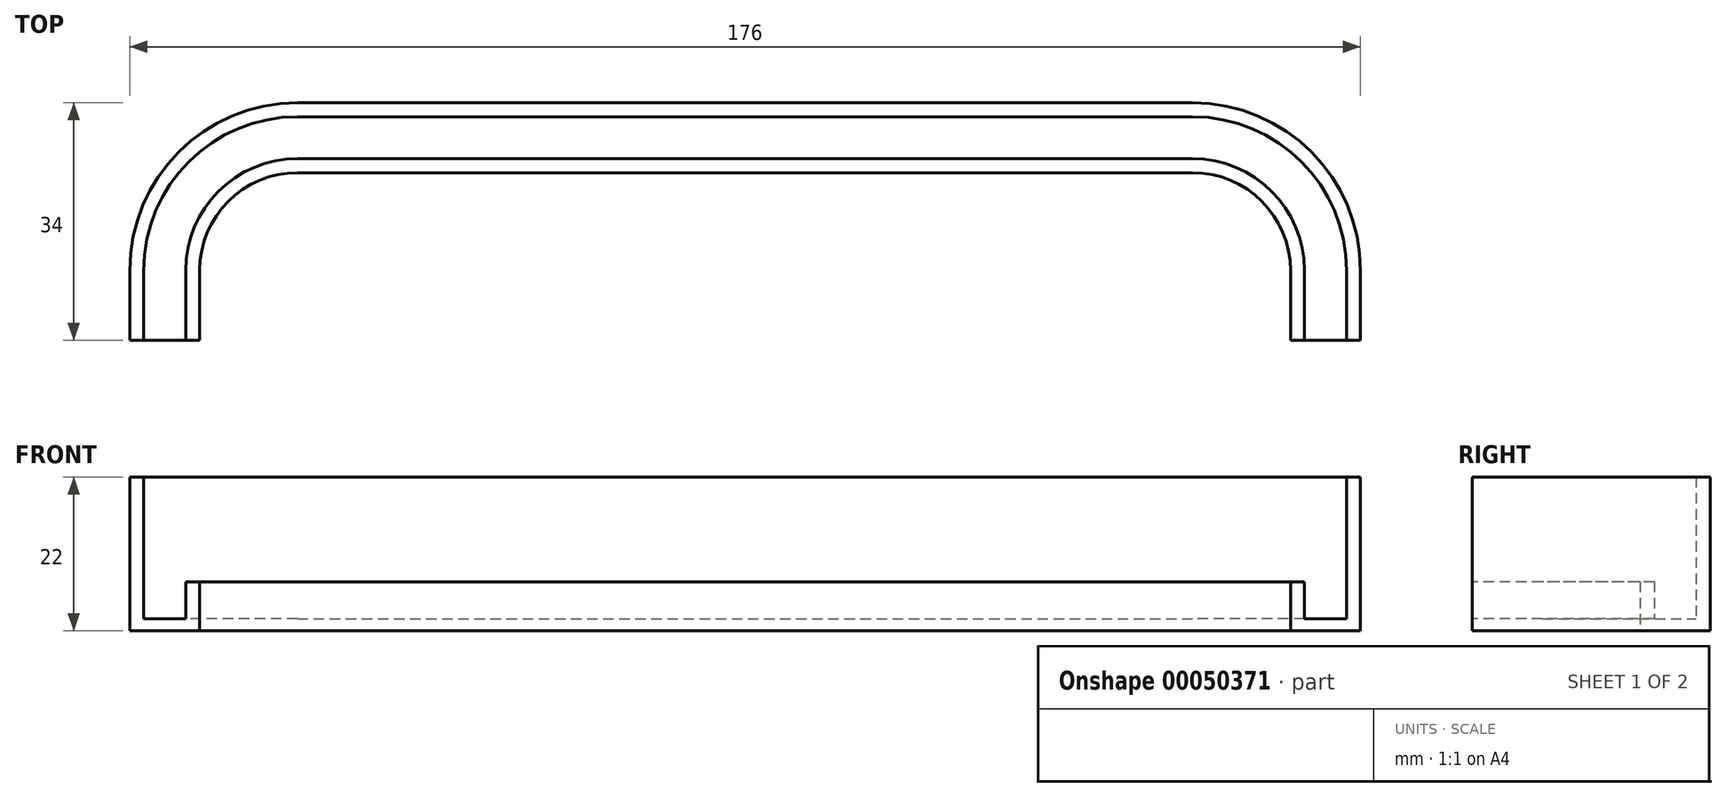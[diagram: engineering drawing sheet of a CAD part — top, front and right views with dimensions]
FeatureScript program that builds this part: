
annotation { "Feature Type Name" : "Feature", "Feature Type Description" : "" }
export const myFeature = defineFeature(function(context is Context, id is Id, definition is map)
    precondition{}
    {
        {
            var Q0;
            Q0=qCreatedBy(makeId("Top.planeOp"),FACE);
            var sketch = newSketch(context, id + "F0", { "sketchPlane" : qUnion([Q0])});
            skLineSegment(sketch, "E0", {"start": v(0, 0) * mm, "end": v(128, 0) * mm});
            skArc(sketch, "E1", {"start": v(0, 0) * mm, "mid": v(-9.9, -4.1) * mm, "end": v(-14, -14) * mm});
            skArc(sketch, "E2", {"start": v(128, 0) * mm, "mid": v(137.9, -4.1) * mm, "end": v(142, -14) * mm});
            skLineSegment(sketch, "E3", {"start": v(-14, -14) * mm, "end": v(-14, -24) * mm});
            skLineSegment(sketch, "E4", {"start": v(142, -14) * mm, "end": v(142, -24) * mm});
            skLineSegment(sketch, "E5.0", {"start": v(-16, -14) * mm, "end": v(-16, -24) * mm});
            skLineSegment(sketch, "E5.1", {"start": v(144, -14) * mm, "end": v(144, -24) * mm});
            skArc(sketch, "E5.2", {"start": v(128, 2) * mm, "mid": v(139.31, -2.69) * mm, "end": v(144, -14) * mm});
            skLineSegment(sketch, "E5.3", {"start": v(0, 2) * mm, "end": v(128, 2) * mm});
            skArc(sketch, "E5.4", {"start": v(0, 2) * mm, "mid": v(-11.31, -2.69) * mm, "end": v(-16, -14) * mm});
            skLineSegment(sketch, "E6.0", {"start": v(-22, -14) * mm, "end": v(-22, -24) * mm});
            skLineSegment(sketch, "E6.1", {"start": v(150, -14) * mm, "end": v(150, -24) * mm});
            skArc(sketch, "E6.2", {"start": v(128, 8) * mm, "mid": v(143.56, 1.56) * mm, "end": v(150, -14) * mm});
            skLineSegment(sketch, "E6.3", {"start": v(0, 8) * mm, "end": v(128, 8) * mm});
            skArc(sketch, "E6.4", {"start": v(0, 8) * mm, "mid": v(-15.56, 1.56) * mm, "end": v(-22, -14) * mm});
            skLineSegment(sketch, "E7.0", {"start": v(-24, -14) * mm, "end": v(-24, -24) * mm});
            skLineSegment(sketch, "E7.1", {"start": v(152, -14) * mm, "end": v(152, -24) * mm});
            skArc(sketch, "E7.2", {"start": v(128, 10) * mm, "mid": v(144.97, 2.97) * mm, "end": v(152, -14) * mm});
            skLineSegment(sketch, "E7.3", {"start": v(0, 10) * mm, "end": v(128, 10) * mm});
            skArc(sketch, "E7.4", {"start": v(0, 10) * mm, "mid": v(-16.97, 2.97) * mm, "end": v(-24, -14) * mm});
            skLineSegment(sketch, "E8", {"start": v(-14, -24) * mm, "end": v(-24, -24) * mm});
            skLineSegment(sketch, "E9", {"start": v(142, -24) * mm, "end": v(152, -24) * mm});
            skSolve(sketch);
        }
        {
            var Q0;
            {var subQ2=sQuery(id+"F0.wireOp",EDGE,"E5.0");Q0=makeQuery(id+"F0.imprint","IMPRINT",FACE,{"disambiguationData":[TD([[makeQuery(id+"F0.imprint","IMPRINT",EDGE,{"derivedFrom":subQ2}),-1.0]])]});}
            extrude(context, id + "F1", {"entities" : qUnion([Q0]), "depth" : 1.7 * mm});
        }
        {
            var Q0;
            Q0=makeQuery(id+"F0.imprint","IMPRINT",FACE,{"disambiguationData":[TD([[makeQuery(id+"F0.imprint","IMPRINT",EDGE,{"derivedFrom":sQuery(id+"F0.wireOp",EDGE,"E0")}),1.0]])]});
            extrude(context, id + "F2", {"entities" : qUnion([Q0]), "operationType" : NewBodyOperationType.ADD, "depth" : 7 * mm});
        }
        {
            var Q0;
            {var subQ2=sQuery(id+"F0.wireOp",EDGE,"E6.0");Q0=makeQuery(id+"F0.imprint","IMPRINT",FACE,{"disambiguationData":[TD([[makeQuery(id+"F0.imprint","IMPRINT",EDGE,{"derivedFrom":subQ2}),-1.0]])]});}
            extrude(context, id + "F3", {"entities" : qUnion([Q0]), "operationType" : NewBodyOperationType.ADD, "depth" : 22 * mm});
        }
    });
